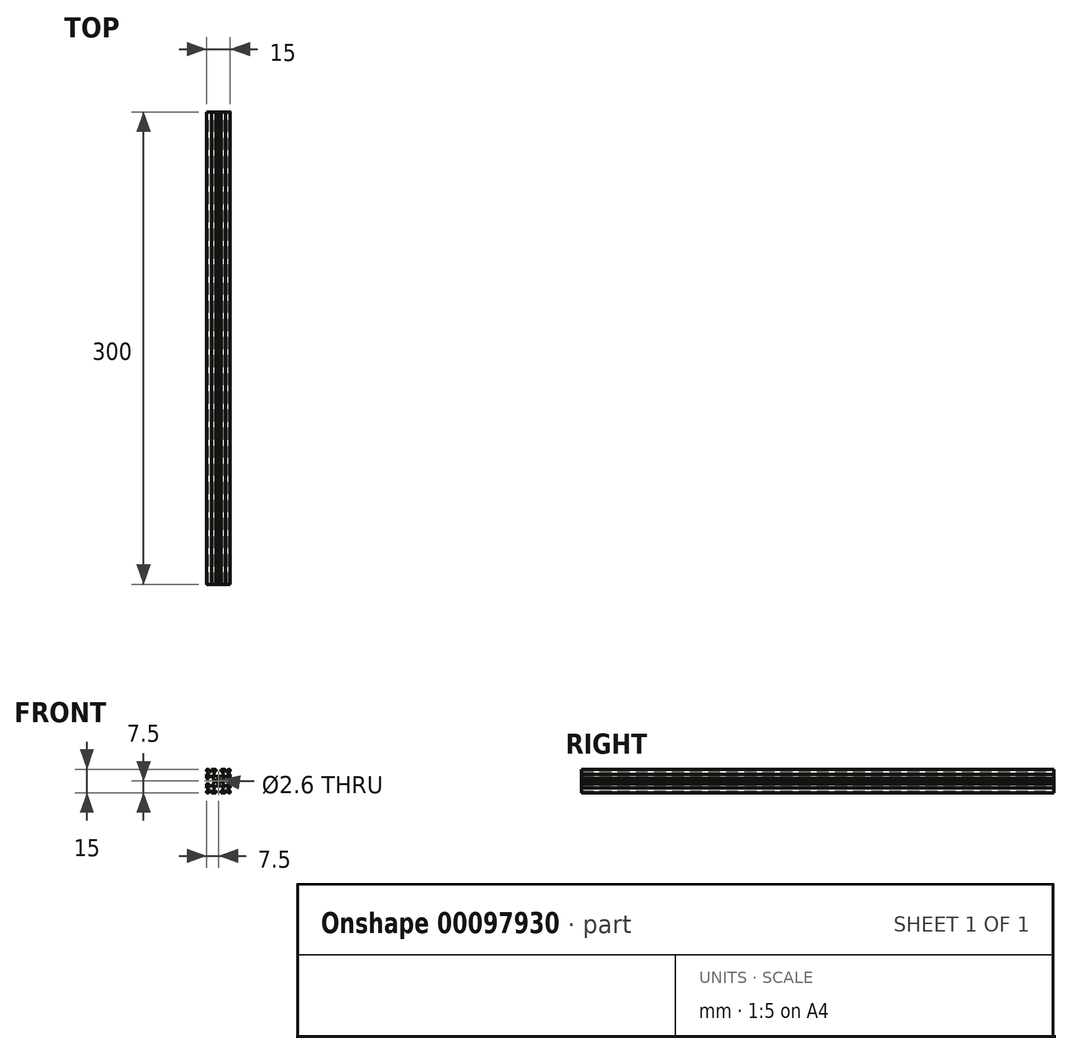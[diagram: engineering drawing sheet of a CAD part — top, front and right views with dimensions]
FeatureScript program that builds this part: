
annotation { "Feature Type Name" : "Feature", "Feature Type Description" : "" }
export const myFeature = defineFeature(function(context is Context, id is Id, definition is map)
    precondition{}
    {
        {
            var Q0;
            Q0=qCreatedBy(makeId("Front.planeOp"),FACE);
            var sketch = newSketch(context, id + "F0", { "sketchPlane" : qUnion([Q0])});
            skLineSegment(sketch, "E0.0.0", {"start": v(0.83, -2.55) * mm, "end": v(0.83, -2.77) * mm});
            skArc(sketch, "E0.0.1", {"start": v(0.83, -2.77) * mm, "mid": v(0.87, -2.9) * mm, "end": v(0.98, -2.97) * mm});
            skLineSegment(sketch, "E0.0.2", {"start": v(0.98, -2.97) * mm, "end": v(2.5, -3.31) * mm});
            skArc(sketch, "E0.0.3", {"start": v(2.5, -3.31) * mm, "mid": v(2.8, -3.49) * mm, "end": v(2.9, -3.8) * mm});
            skLineSegment(sketch, "E0.0.4", {"start": v(2.9, -3.8) * mm, "end": v(2.9, -5.9) * mm});
            skArc(sketch, "E0.0.5", {"start": v(2.9, -5.9) * mm, "mid": v(2.84, -6.04) * mm, "end": v(2.7, -6.1) * mm});
            skLineSegment(sketch, "E0.0.6", {"start": v(2.7, -6.1) * mm, "end": v(2.1, -6.1) * mm});
            skArc(sketch, "E0.0.7", {"start": v(2.1, -6.1) * mm, "mid": v(1.75, -6.25) * mm, "end": v(1.6, -6.6) * mm});
            skLineSegment(sketch, "E0.0.8", {"start": v(1.6, -6.6) * mm, "end": v(1.6, -7) * mm});
            skArc(sketch, "E0.0.9", {"start": v(1.6, -7) * mm, "mid": v(1.75, -7.35) * mm, "end": v(2.1, -7.5) * mm});
            skLineSegment(sketch, "E0.0.10", {"start": v(2.1, -7.5) * mm, "end": v(3.9, -7.5) * mm});
            skArc(sketch, "E0.0.11", {"start": v(3.9, -7.5) * mm, "mid": v(4.25, -7.35) * mm, "end": v(4.4, -7) * mm});
            skLineSegment(sketch, "E0.0.12", {"start": v(4.4, -7) * mm, "end": v(4.4, -6.67) * mm});
            skArc(sketch, "E0.0.13", {"start": v(4.4, -6.67) * mm, "mid": v(4.7, -6.2) * mm, "end": v(5.25, -6.31) * mm});
            skLineSegment(sketch, "E0.0.14", {"start": v(5.25, -6.31) * mm, "end": v(6.3, -7.35) * mm});
            skArc(sketch, "E0.0.15", {"start": v(6.3, -7.35) * mm, "mid": v(6.46, -7.46) * mm, "end": v(6.65, -7.5) * mm});
            skLineSegment(sketch, "E0.0.16", {"start": v(6.65, -7.5) * mm, "end": v(7.25, -7.5) * mm});
            skArc(sketch, "E0.0.17", {"start": v(7.25, -7.5) * mm, "mid": v(7.43, -7.43) * mm, "end": v(7.5, -7.25) * mm});
            skLineSegment(sketch, "E0.0.18", {"start": v(7.5, -7.25) * mm, "end": v(7.5, -6.65) * mm});
            skArc(sketch, "E0.0.19", {"start": v(7.5, -6.65) * mm, "mid": v(7.46, -6.46) * mm, "end": v(7.35, -6.3) * mm});
            skLineSegment(sketch, "E0.0.20", {"start": v(7.35, -6.3) * mm, "end": v(6.31, -5.25) * mm});
            skArc(sketch, "E0.0.21", {"start": v(6.31, -5.25) * mm, "mid": v(6.2, -4.7) * mm, "end": v(6.67, -4.4) * mm});
            skLineSegment(sketch, "E0.0.22", {"start": v(6.67, -4.4) * mm, "end": v(7, -4.4) * mm});
            skArc(sketch, "E0.0.23", {"start": v(7, -4.4) * mm, "mid": v(7.35, -4.25) * mm, "end": v(7.5, -3.9) * mm});
            skLineSegment(sketch, "E0.0.24", {"start": v(7.5, -3.9) * mm, "end": v(7.5, -2.1) * mm});
            skArc(sketch, "E0.0.25", {"start": v(7.5, -2.1) * mm, "mid": v(7.35, -1.75) * mm, "end": v(7, -1.6) * mm});
            skLineSegment(sketch, "E0.0.26", {"start": v(7, -1.6) * mm, "end": v(6.6, -1.6) * mm});
            skArc(sketch, "E0.0.27", {"start": v(6.6, -1.6) * mm, "mid": v(6.25, -1.75) * mm, "end": v(6.1, -2.1) * mm});
            skLineSegment(sketch, "E0.0.28", {"start": v(6.1, -2.1) * mm, "end": v(6.1, -2.7) * mm});
            skArc(sketch, "E0.0.29", {"start": v(6.1, -2.7) * mm, "mid": v(6.04, -2.84) * mm, "end": v(5.9, -2.9) * mm});
            skLineSegment(sketch, "E0.0.30", {"start": v(5.9, -2.9) * mm, "end": v(3.8, -2.9) * mm});
            skArc(sketch, "E0.0.31", {"start": v(3.8, -2.9) * mm, "mid": v(3.49, -2.8) * mm, "end": v(3.31, -2.5) * mm});
            skLineSegment(sketch, "E0.0.32", {"start": v(3.31, -2.5) * mm, "end": v(2.97, -0.98) * mm});
            skArc(sketch, "E0.0.33", {"start": v(2.97, -0.98) * mm, "mid": v(2.9, -0.87) * mm, "end": v(2.77, -0.83) * mm});
            skLineSegment(sketch, "E0.0.34", {"start": v(2.77, -0.83) * mm, "end": v(2.55, -0.83) * mm});
            skArc(sketch, "E0.0.35", {"start": v(2.55, -0.83) * mm, "mid": v(2.4, -0.77) * mm, "end": v(2.35, -0.63) * mm});
            skLineSegment(sketch, "E0.0.36", {"start": v(2.35, -0.63) * mm, "end": v(2.35, 0.63) * mm});
            skArc(sketch, "E0.0.37", {"start": v(2.35, 0.63) * mm, "mid": v(2.4, 0.77) * mm, "end": v(2.55, 0.83) * mm});
            skLineSegment(sketch, "E0.0.38", {"start": v(2.55, 0.83) * mm, "end": v(2.77, 0.83) * mm});
            skArc(sketch, "E0.0.39", {"start": v(2.77, 0.83) * mm, "mid": v(2.9, 0.87) * mm, "end": v(2.97, 0.98) * mm});
            skLineSegment(sketch, "E0.0.40", {"start": v(2.97, 0.98) * mm, "end": v(3.31, 2.5) * mm});
            skArc(sketch, "E0.0.41", {"start": v(3.31, 2.5) * mm, "mid": v(3.49, 2.8) * mm, "end": v(3.8, 2.9) * mm});
            skLineSegment(sketch, "E0.0.42", {"start": v(3.8, 2.9) * mm, "end": v(5.9, 2.9) * mm});
            skArc(sketch, "E0.0.43", {"start": v(5.9, 2.9) * mm, "mid": v(6.04, 2.84) * mm, "end": v(6.1, 2.7) * mm});
            skLineSegment(sketch, "E0.0.44", {"start": v(6.1, 2.7) * mm, "end": v(6.1, 2.1) * mm});
            skArc(sketch, "E0.0.45", {"start": v(6.1, 2.1) * mm, "mid": v(6.25, 1.75) * mm, "end": v(6.6, 1.6) * mm});
            skLineSegment(sketch, "E0.0.46", {"start": v(6.6, 1.6) * mm, "end": v(7, 1.6) * mm});
            skArc(sketch, "E0.0.47", {"start": v(7, 1.6) * mm, "mid": v(7.35, 1.75) * mm, "end": v(7.5, 2.1) * mm});
            skLineSegment(sketch, "E0.0.48", {"start": v(7.5, 2.1) * mm, "end": v(7.5, 3.9) * mm});
            skArc(sketch, "E0.0.49", {"start": v(7.5, 3.9) * mm, "mid": v(7.35, 4.25) * mm, "end": v(7, 4.4) * mm});
            skLineSegment(sketch, "E0.0.50", {"start": v(7, 4.4) * mm, "end": v(6.67, 4.4) * mm});
            skArc(sketch, "E0.0.51", {"start": v(6.67, 4.4) * mm, "mid": v(6.2, 4.7) * mm, "end": v(6.31, 5.25) * mm});
            skLineSegment(sketch, "E0.0.52", {"start": v(6.31, 5.25) * mm, "end": v(7.35, 6.3) * mm});
            skArc(sketch, "E0.0.53", {"start": v(7.35, 6.3) * mm, "mid": v(7.46, 6.46) * mm, "end": v(7.5, 6.65) * mm});
            skLineSegment(sketch, "E0.0.54", {"start": v(7.5, 6.65) * mm, "end": v(7.5, 7.25) * mm});
            skArc(sketch, "E0.0.55", {"start": v(7.5, 7.25) * mm, "mid": v(7.43, 7.43) * mm, "end": v(7.25, 7.5) * mm});
            skLineSegment(sketch, "E0.0.56", {"start": v(7.25, 7.5) * mm, "end": v(6.65, 7.5) * mm});
            skArc(sketch, "E0.0.57", {"start": v(6.65, 7.5) * mm, "mid": v(6.46, 7.46) * mm, "end": v(6.3, 7.35) * mm});
            skLineSegment(sketch, "E0.0.58", {"start": v(6.3, 7.35) * mm, "end": v(5.25, 6.31) * mm});
            skArc(sketch, "E0.0.59", {"start": v(5.25, 6.31) * mm, "mid": v(4.7, 6.2) * mm, "end": v(4.4, 6.67) * mm});
            skLineSegment(sketch, "E0.0.60", {"start": v(4.4, 6.67) * mm, "end": v(4.4, 7) * mm});
            skArc(sketch, "E0.0.61", {"start": v(4.4, 7) * mm, "mid": v(4.25, 7.35) * mm, "end": v(3.9, 7.5) * mm});
            skLineSegment(sketch, "E0.0.62", {"start": v(3.9, 7.5) * mm, "end": v(2.1, 7.5) * mm});
            skArc(sketch, "E0.0.63", {"start": v(2.1, 7.5) * mm, "mid": v(1.75, 7.35) * mm, "end": v(1.6, 7) * mm});
            skLineSegment(sketch, "E0.0.64", {"start": v(1.6, 7) * mm, "end": v(1.6, 6.6) * mm});
            skArc(sketch, "E0.0.65", {"start": v(1.6, 6.6) * mm, "mid": v(1.75, 6.25) * mm, "end": v(2.1, 6.1) * mm});
            skLineSegment(sketch, "E0.0.66", {"start": v(2.1, 6.1) * mm, "end": v(2.7, 6.1) * mm});
            skArc(sketch, "E0.0.67", {"start": v(2.7, 6.1) * mm, "mid": v(2.84, 6.04) * mm, "end": v(2.9, 5.9) * mm});
            skLineSegment(sketch, "E0.0.68", {"start": v(2.9, 5.9) * mm, "end": v(2.9, 3.8) * mm});
            skArc(sketch, "E0.0.69", {"start": v(2.9, 3.8) * mm, "mid": v(2.8, 3.49) * mm, "end": v(2.5, 3.31) * mm});
            skLineSegment(sketch, "E0.0.70", {"start": v(2.5, 3.31) * mm, "end": v(0.98, 2.97) * mm});
            skArc(sketch, "E0.0.71", {"start": v(0.98, 2.97) * mm, "mid": v(0.87, 2.9) * mm, "end": v(0.83, 2.77) * mm});
            skLineSegment(sketch, "E0.0.72", {"start": v(0.83, 2.77) * mm, "end": v(0.83, 2.55) * mm});
            skArc(sketch, "E0.0.73", {"start": v(0.83, 2.55) * mm, "mid": v(0.77, 2.4) * mm, "end": v(0.63, 2.35) * mm});
            skLineSegment(sketch, "E0.0.74", {"start": v(0.63, 2.35) * mm, "end": v(-0.63, 2.35) * mm});
            skArc(sketch, "E0.0.75", {"start": v(-0.63, 2.35) * mm, "mid": v(-0.77, 2.4) * mm, "end": v(-0.83, 2.55) * mm});
            skLineSegment(sketch, "E0.0.76", {"start": v(-0.83, 2.55) * mm, "end": v(-0.83, 2.77) * mm});
            skArc(sketch, "E0.0.77", {"start": v(-0.83, 2.77) * mm, "mid": v(-0.87, 2.9) * mm, "end": v(-0.98, 2.97) * mm});
            skLineSegment(sketch, "E0.0.78", {"start": v(-0.98, 2.97) * mm, "end": v(-2.5, 3.31) * mm});
            skArc(sketch, "E0.0.79", {"start": v(-2.5, 3.31) * mm, "mid": v(-2.8, 3.49) * mm, "end": v(-2.9, 3.8) * mm});
            skLineSegment(sketch, "E0.0.80", {"start": v(-2.9, 3.8) * mm, "end": v(-2.9, 5.9) * mm});
            skArc(sketch, "E0.0.81", {"start": v(-2.9, 5.9) * mm, "mid": v(-2.84, 6.04) * mm, "end": v(-2.7, 6.1) * mm});
            skLineSegment(sketch, "E0.0.82", {"start": v(-2.7, 6.1) * mm, "end": v(-2.1, 6.1) * mm});
            skArc(sketch, "E0.0.83", {"start": v(-2.1, 6.1) * mm, "mid": v(-1.75, 6.25) * mm, "end": v(-1.6, 6.6) * mm});
            skLineSegment(sketch, "E0.0.84", {"start": v(-1.6, 6.6) * mm, "end": v(-1.6, 7) * mm});
            skArc(sketch, "E0.0.85", {"start": v(-1.6, 7) * mm, "mid": v(-1.75, 7.35) * mm, "end": v(-2.1, 7.5) * mm});
            skLineSegment(sketch, "E0.0.86", {"start": v(-2.1, 7.5) * mm, "end": v(-3.9, 7.5) * mm});
            skArc(sketch, "E0.0.87", {"start": v(-3.9, 7.5) * mm, "mid": v(-4.25, 7.35) * mm, "end": v(-4.4, 7) * mm});
            skLineSegment(sketch, "E0.0.88", {"start": v(-4.4, 7) * mm, "end": v(-4.4, 6.67) * mm});
            skArc(sketch, "E0.0.89", {"start": v(-4.4, 6.67) * mm, "mid": v(-4.7, 6.2) * mm, "end": v(-5.25, 6.31) * mm});
            skLineSegment(sketch, "E0.0.90", {"start": v(-5.25, 6.31) * mm, "end": v(-6.3, 7.35) * mm});
            skArc(sketch, "E0.0.91", {"start": v(-6.3, 7.35) * mm, "mid": v(-6.46, 7.46) * mm, "end": v(-6.65, 7.5) * mm});
            skLineSegment(sketch, "E0.0.92", {"start": v(-6.65, 7.5) * mm, "end": v(-7.25, 7.5) * mm});
            skArc(sketch, "E0.0.93", {"start": v(-7.25, 7.5) * mm, "mid": v(-7.43, 7.43) * mm, "end": v(-7.5, 7.25) * mm});
            skLineSegment(sketch, "E0.0.94", {"start": v(-7.5, 7.25) * mm, "end": v(-7.5, 6.65) * mm});
            skArc(sketch, "E0.0.95", {"start": v(-7.5, 6.65) * mm, "mid": v(-7.46, 6.46) * mm, "end": v(-7.35, 6.3) * mm});
            skLineSegment(sketch, "E0.0.96", {"start": v(-7.35, 6.3) * mm, "end": v(-6.31, 5.25) * mm});
            skArc(sketch, "E0.0.97", {"start": v(-6.31, 5.25) * mm, "mid": v(-6.2, 4.7) * mm, "end": v(-6.67, 4.4) * mm});
            skLineSegment(sketch, "E0.0.98", {"start": v(-6.67, 4.4) * mm, "end": v(-7, 4.4) * mm});
            skArc(sketch, "E0.0.99", {"start": v(-7, 4.4) * mm, "mid": v(-7.35, 4.25) * mm, "end": v(-7.5, 3.9) * mm});
            skLineSegment(sketch, "E0.0.100", {"start": v(-7.5, 3.9) * mm, "end": v(-7.5, 2.1) * mm});
            skArc(sketch, "E0.0.101", {"start": v(-7.5, 2.1) * mm, "mid": v(-7.35, 1.75) * mm, "end": v(-7, 1.6) * mm});
            skLineSegment(sketch, "E0.0.102", {"start": v(-7, 1.6) * mm, "end": v(-6.6, 1.6) * mm});
            skArc(sketch, "E0.0.103", {"start": v(-6.6, 1.6) * mm, "mid": v(-6.25, 1.75) * mm, "end": v(-6.1, 2.1) * mm});
            skLineSegment(sketch, "E0.0.104", {"start": v(-6.1, 2.1) * mm, "end": v(-6.1, 2.7) * mm});
            skArc(sketch, "E0.0.105", {"start": v(-6.1, 2.7) * mm, "mid": v(-6.04, 2.84) * mm, "end": v(-5.9, 2.9) * mm});
            skLineSegment(sketch, "E0.0.106", {"start": v(-5.9, 2.9) * mm, "end": v(-3.8, 2.9) * mm});
            skArc(sketch, "E0.0.107", {"start": v(-3.8, 2.9) * mm, "mid": v(-3.49, 2.8) * mm, "end": v(-3.31, 2.5) * mm});
            skLineSegment(sketch, "E0.0.108", {"start": v(-3.31, 2.5) * mm, "end": v(-2.97, 0.98) * mm});
            skArc(sketch, "E0.0.109", {"start": v(-2.97, 0.98) * mm, "mid": v(-2.9, 0.87) * mm, "end": v(-2.77, 0.83) * mm});
            skLineSegment(sketch, "E0.0.110", {"start": v(-2.77, 0.83) * mm, "end": v(-2.55, 0.83) * mm});
            skArc(sketch, "E0.0.111", {"start": v(-2.55, 0.83) * mm, "mid": v(-2.4, 0.77) * mm, "end": v(-2.35, 0.63) * mm});
            skLineSegment(sketch, "E0.0.112", {"start": v(-2.35, 0.63) * mm, "end": v(-2.35, -0.63) * mm});
            skArc(sketch, "E0.0.113", {"start": v(-2.35, -0.63) * mm, "mid": v(-2.4, -0.77) * mm, "end": v(-2.55, -0.83) * mm});
            skLineSegment(sketch, "E0.0.114", {"start": v(-2.55, -0.83) * mm, "end": v(-2.77, -0.83) * mm});
            skArc(sketch, "E0.0.115", {"start": v(-2.77, -0.83) * mm, "mid": v(-2.9, -0.87) * mm, "end": v(-2.97, -0.98) * mm});
            skLineSegment(sketch, "E0.0.116", {"start": v(-2.97, -0.98) * mm, "end": v(-3.31, -2.5) * mm});
            skArc(sketch, "E0.0.117", {"start": v(-3.31, -2.5) * mm, "mid": v(-3.49, -2.8) * mm, "end": v(-3.8, -2.9) * mm});
            skLineSegment(sketch, "E0.0.118", {"start": v(-3.8, -2.9) * mm, "end": v(-5.9, -2.9) * mm});
            skArc(sketch, "E0.0.119", {"start": v(-5.9, -2.9) * mm, "mid": v(-6.04, -2.84) * mm, "end": v(-6.1, -2.7) * mm});
            skLineSegment(sketch, "E0.0.120", {"start": v(-6.1, -2.7) * mm, "end": v(-6.1, -2.1) * mm});
            skArc(sketch, "E0.0.121", {"start": v(-6.1, -2.1) * mm, "mid": v(-6.25, -1.75) * mm, "end": v(-6.6, -1.6) * mm});
            skLineSegment(sketch, "E0.0.122", {"start": v(-6.6, -1.6) * mm, "end": v(-7, -1.6) * mm});
            skArc(sketch, "E0.0.123", {"start": v(-7, -1.6) * mm, "mid": v(-7.35, -1.75) * mm, "end": v(-7.5, -2.1) * mm});
            skLineSegment(sketch, "E0.0.124", {"start": v(-7.5, -2.1) * mm, "end": v(-7.5, -3.9) * mm});
            skArc(sketch, "E0.0.125", {"start": v(-7.5, -3.9) * mm, "mid": v(-7.35, -4.25) * mm, "end": v(-7, -4.4) * mm});
            skLineSegment(sketch, "E0.0.126", {"start": v(-7, -4.4) * mm, "end": v(-6.67, -4.4) * mm});
            skArc(sketch, "E0.0.127", {"start": v(-6.67, -4.4) * mm, "mid": v(-6.2, -4.7) * mm, "end": v(-6.31, -5.25) * mm});
            skLineSegment(sketch, "E0.0.128", {"start": v(-6.31, -5.25) * mm, "end": v(-7.35, -6.3) * mm});
            skArc(sketch, "E0.0.129", {"start": v(-7.35, -6.3) * mm, "mid": v(-7.46, -6.46) * mm, "end": v(-7.5, -6.65) * mm});
            skLineSegment(sketch, "E0.0.130", {"start": v(-7.5, -6.65) * mm, "end": v(-7.5, -7.25) * mm});
            skArc(sketch, "E0.0.131", {"start": v(-7.5, -7.25) * mm, "mid": v(-7.43, -7.43) * mm, "end": v(-7.25, -7.5) * mm});
            skLineSegment(sketch, "E0.0.132", {"start": v(-7.25, -7.5) * mm, "end": v(-6.65, -7.5) * mm});
            skArc(sketch, "E0.0.133", {"start": v(-6.65, -7.5) * mm, "mid": v(-6.46, -7.46) * mm, "end": v(-6.3, -7.35) * mm});
            skLineSegment(sketch, "E0.0.134", {"start": v(-6.3, -7.35) * mm, "end": v(-5.25, -6.31) * mm});
            skArc(sketch, "E0.0.135", {"start": v(-5.25, -6.31) * mm, "mid": v(-4.7, -6.2) * mm, "end": v(-4.4, -6.67) * mm});
            skLineSegment(sketch, "E0.0.136", {"start": v(-4.4, -6.67) * mm, "end": v(-4.4, -7) * mm});
            skArc(sketch, "E0.0.137", {"start": v(-4.4, -7) * mm, "mid": v(-4.25, -7.35) * mm, "end": v(-3.9, -7.5) * mm});
            skLineSegment(sketch, "E0.0.138", {"start": v(-3.9, -7.5) * mm, "end": v(-2.1, -7.5) * mm});
            skArc(sketch, "E0.0.139", {"start": v(-2.1, -7.5) * mm, "mid": v(-1.75, -7.35) * mm, "end": v(-1.6, -7) * mm});
            skLineSegment(sketch, "E0.0.140", {"start": v(-1.6, -7) * mm, "end": v(-1.6, -6.6) * mm});
            skArc(sketch, "E0.0.141", {"start": v(-1.6, -6.6) * mm, "mid": v(-1.75, -6.25) * mm, "end": v(-2.1, -6.1) * mm});
            skLineSegment(sketch, "E0.0.142", {"start": v(-2.1, -6.1) * mm, "end": v(-2.7, -6.1) * mm});
            skArc(sketch, "E0.0.143", {"start": v(-2.7, -6.1) * mm, "mid": v(-2.84, -6.04) * mm, "end": v(-2.9, -5.9) * mm});
            skLineSegment(sketch, "E0.0.144", {"start": v(-2.9, -5.9) * mm, "end": v(-2.9, -3.8) * mm});
            skArc(sketch, "E0.0.145", {"start": v(-2.9, -3.8) * mm, "mid": v(-2.8, -3.49) * mm, "end": v(-2.5, -3.31) * mm});
            skLineSegment(sketch, "E0.0.146", {"start": v(-2.5, -3.31) * mm, "end": v(-0.98, -2.97) * mm});
            skArc(sketch, "E0.0.147", {"start": v(-0.98, -2.97) * mm, "mid": v(-0.87, -2.9) * mm, "end": v(-0.83, -2.77) * mm});
            skLineSegment(sketch, "E0.0.148", {"start": v(-0.83, -2.77) * mm, "end": v(-0.83, -2.55) * mm});
            skArc(sketch, "E0.0.149", {"start": v(-0.83, -2.55) * mm, "mid": v(-0.77, -2.4) * mm, "end": v(-0.63, -2.35) * mm});
            skLineSegment(sketch, "E0.0.150", {"start": v(-0.63, -2.35) * mm, "end": v(0.63, -2.35) * mm});
            skArc(sketch, "E0.0.151", {"start": v(0.63, -2.35) * mm, "mid": v(0.77, -2.4) * mm, "end": v(0.83, -2.55) * mm});
            skPoint(sketch, "E1", {"position": v(0, 0) * mm});
            skPoint(sketch, "E1.positionSnap0", {"position": v(0, 2.35) * mm});
            skPoint(sketch, "E1.positionSnap1", {"position": v(2.35, 0) * mm});
            skCircle(sketch, "E2", {"center": v(0, 0) * mm, "radius": 1.3 * mm});
            skSolve(sketch);
        }
        {
            var Q0;
            Q0=makeQuery(id+"F0.imprint","IMPRINT",FACE,{"disambiguationData":[TD([[makeQuery(id+"F0.imprint","IMPRINT",EDGE,{"derivedFrom":sQuery(id+"F0.wireOp",EDGE,"E0.0.0")}),1.0]])]});
            extrude(context, id + "F1", {"entities" : qUnion([Q0]), "endBound" : BoundingType.SYMMETRIC, "depth" : 300 * mm});
        }
    });
